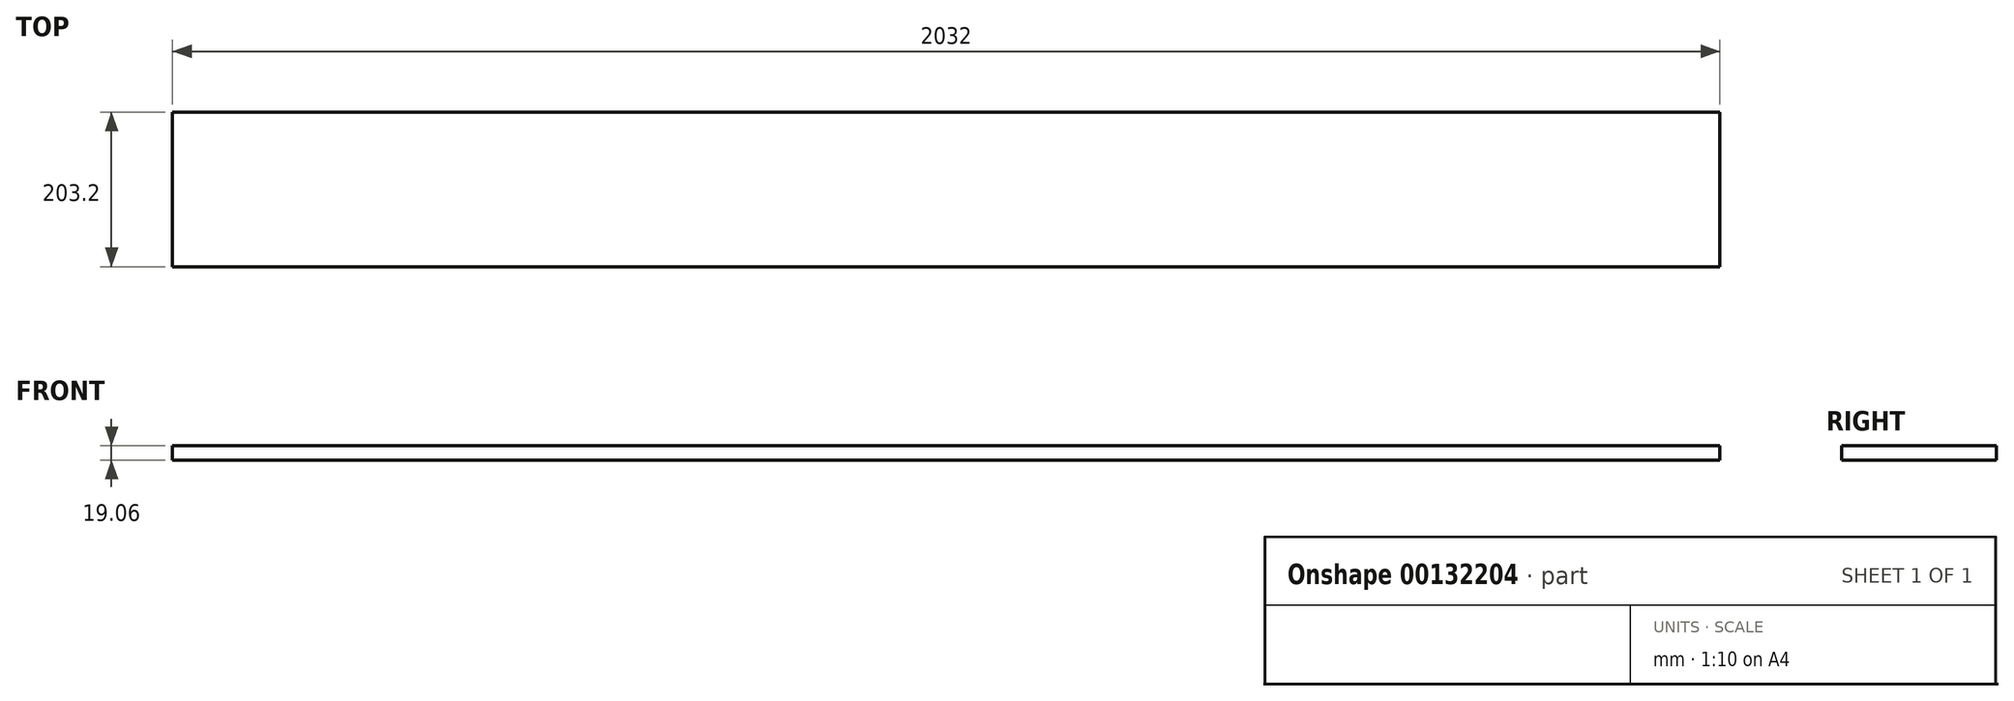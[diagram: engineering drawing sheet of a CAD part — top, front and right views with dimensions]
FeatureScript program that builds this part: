
annotation { "Feature Type Name" : "Feature", "Feature Type Description" : "" }
export const myFeature = defineFeature(function(context is Context, id is Id, definition is map)
    precondition{}
    {
        {
            var Q0;
            Q0=qCreatedBy(makeId("Top.planeOp"),FACE);
            var sketch = newSketch(context, id + "F0", { "sketchPlane" : qUnion([Q0])});
            skLineSegment(sketch, "E0.bottom", {"start": v(-1016, -101.6) * mm, "end": v(1016, -101.6) * mm});
            skLineSegment(sketch, "E0.top", {"start": v(-1016, 101.6) * mm, "end": v(1016, 101.6) * mm});
            skLineSegment(sketch, "E0.left", {"start": v(-1016, -101.6) * mm, "end": v(-1016, 101.6) * mm});
            skLineSegment(sketch, "E0.right", {"start": v(1016, -101.6) * mm, "end": v(1016, 101.6) * mm});
            skPoint(sketch, "E0.middle", {"position": v(0, 0) * mm});
            skSolve(sketch);
        }
        {
            var Q0;
            Q0=makeQuery(id+"F0.imprint","IMPRINT",FACE,{"disambiguationData":[TD([[makeQuery(id+"F0.imprint","IMPRINT",EDGE,{"derivedFrom":sQuery(id+"F0.wireOp",EDGE,"E0.bottom")}),1.0]])]});
            extrude(context, id + "F1", {"entities" : qUnion([Q0]), "endBound" : BoundingType.SYMMETRIC, "depth" : 19.05 * mm});
        }
    });
